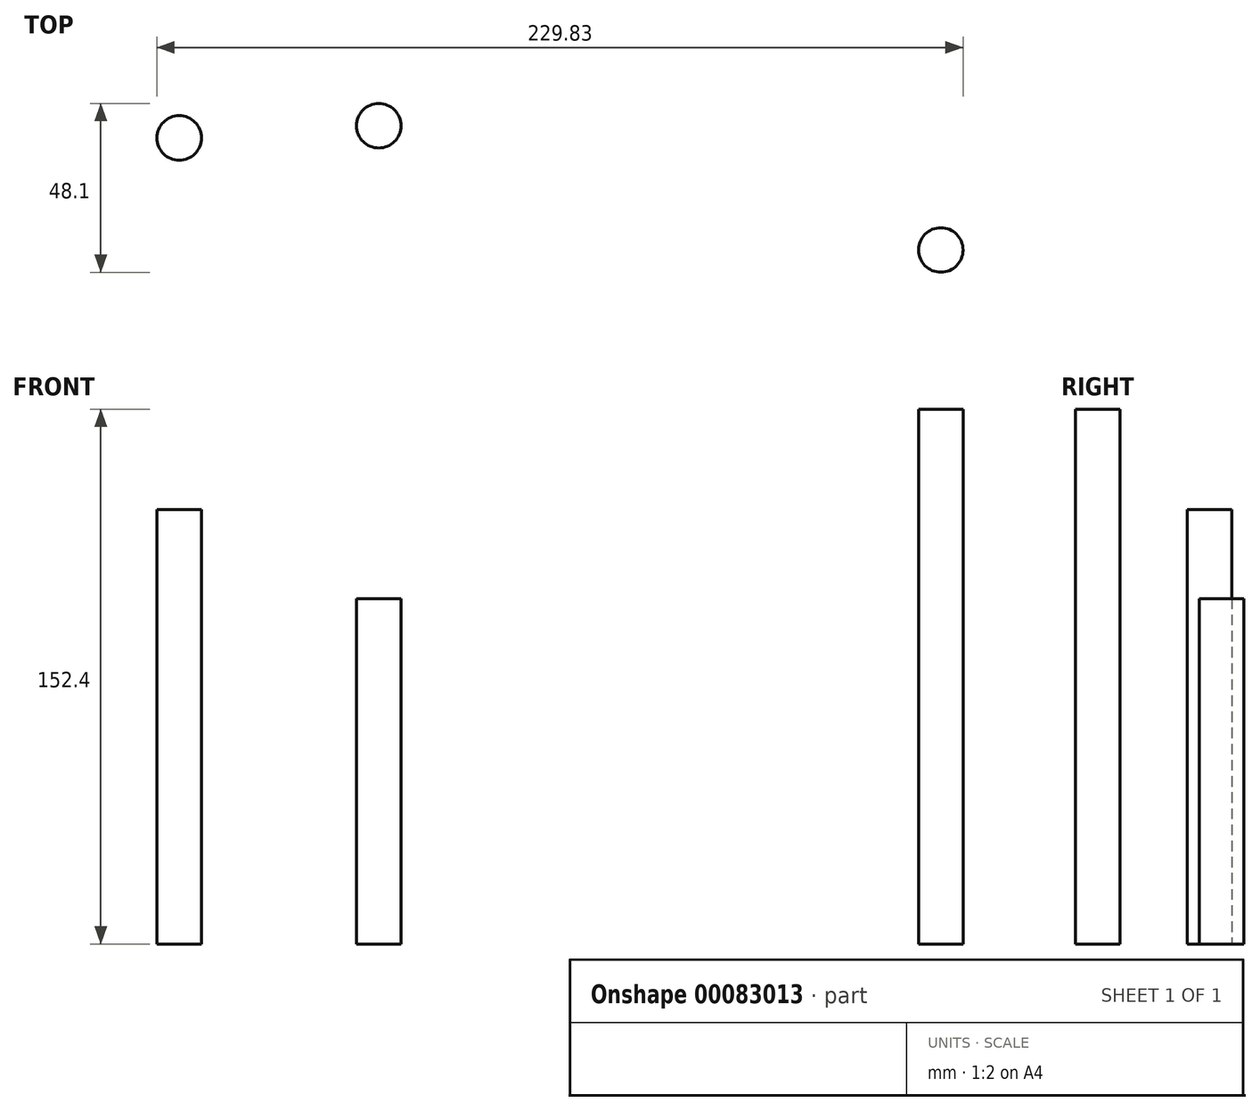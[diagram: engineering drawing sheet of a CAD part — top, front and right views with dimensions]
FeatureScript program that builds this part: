
annotation { "Feature Type Name" : "Feature", "Feature Type Description" : "" }
export const myFeature = defineFeature(function(context is Context, id is Id, definition is map)
    precondition{}
    {
        {
            var Q0;
            Q0=qCreatedBy(makeId("Top.planeOp"),FACE);
            var sketch = newSketch(context, id + "F0", { "sketchPlane" : qUnion([Q0])});
            skCircle(sketch, "E0", {"center": v(208.06, 3.86) * mm, "radius": 6.34 * mm});
            skSolve(sketch);
        }
        {
            var Q0;
            Q0=makeQuery(id+"F0.imprint","IMPRINT",FACE,{"disambiguationData":[TD([[makeQuery(id+"F0.imprint","IMPRINT",EDGE,{"derivedFrom":sQuery(id+"F0.wireOp",EDGE,"E0")}),1.0]])]});
            extrude(context, id + "F1", {"entities" : qUnion([Q0]), "depth" : 152.4 * mm});
        }
        {
            var Q0;
            Q0=qCreatedBy(makeId("Top.planeOp"),FACE);
            var sketch = newSketch(context, id + "F2", { "sketchPlane" : qUnion([Q0])});
            skCircle(sketch, "E1", {"center": v(47.82, 39.26) * mm, "radius": 6.35 * mm});
            skSolve(sketch);
        }
        {
            var Q0;
            Q0=makeQuery(id+"F2.imprint","IMPRINT",FACE,{"disambiguationData":[TD([[makeQuery(id+"F2.imprint","IMPRINT",EDGE,{"derivedFrom":sQuery(id+"F2.wireOp",EDGE,"E1")}),1.0]])]});
            extrude(context, id + "F3", {"entities" : qUnion([Q0]), "depth" : 98.42 * mm});
        }
        {
            var Q0;
            Q0=qCreatedBy(makeId("Top.planeOp"),FACE);
            var sketch = newSketch(context, id + "F4", { "sketchPlane" : qUnion([Q0])});
            skCircle(sketch, "E2", {"center": v(-9.07, 35.77) * mm, "radius": 6.35 * mm});
            skSolve(sketch);
        }
        {
            var Q0;
            Q0=makeQuery(id+"F4.imprint","IMPRINT",FACE,{"disambiguationData":[TD([[makeQuery(id+"F4.imprint","IMPRINT",EDGE,{"derivedFrom":sQuery(id+"F4.wireOp",EDGE,"E2")}),1.0]])]});
            extrude(context, id + "F5", {"entities" : qUnion([Q0]), "depth" : 123.82 * mm});
        }
    });
